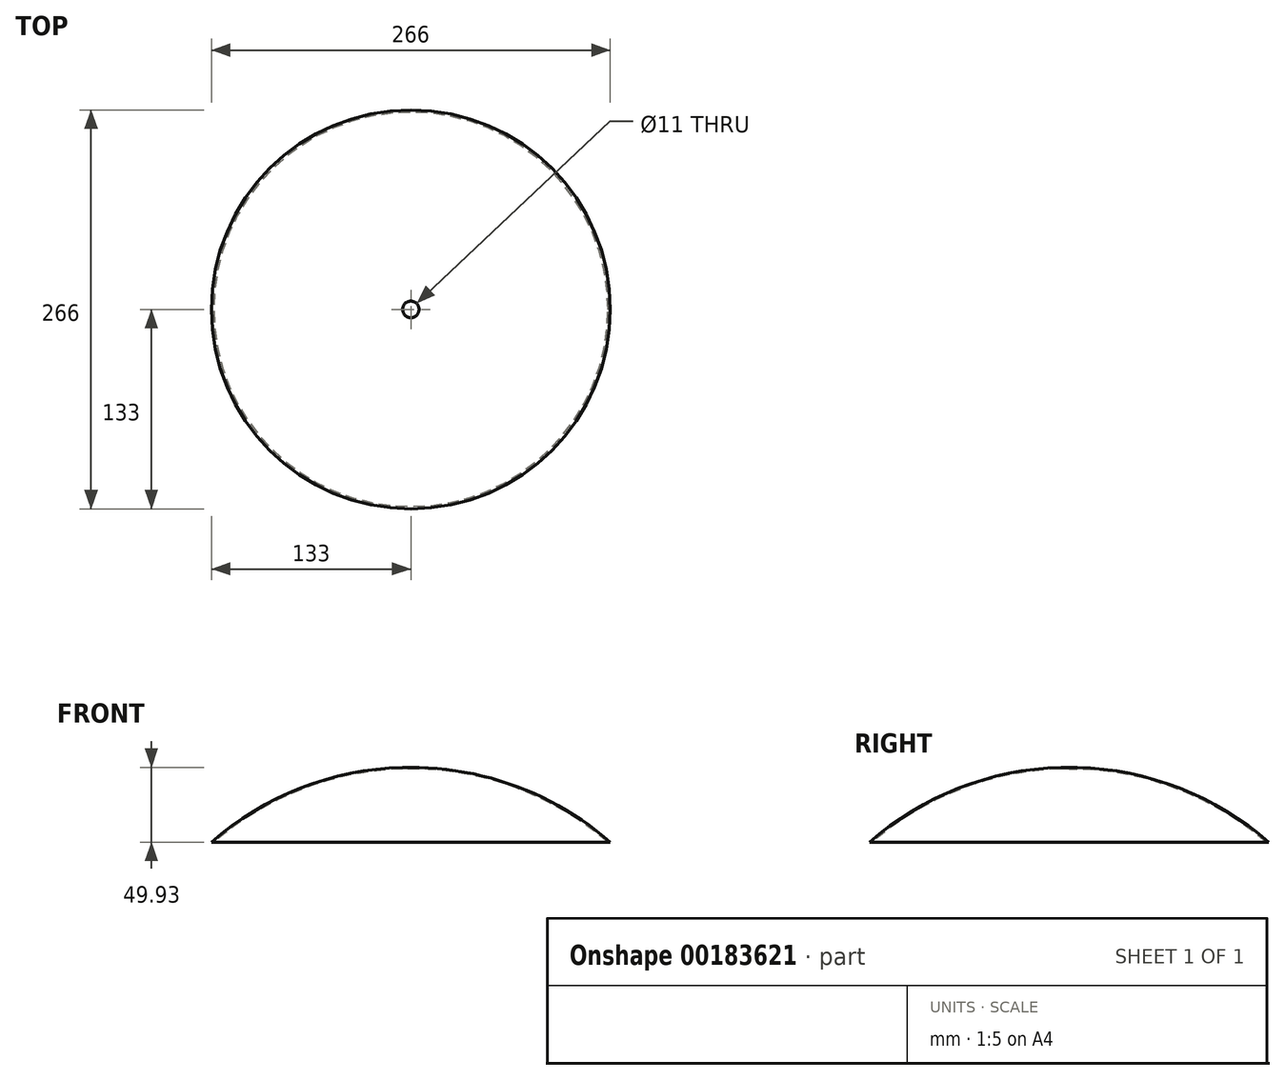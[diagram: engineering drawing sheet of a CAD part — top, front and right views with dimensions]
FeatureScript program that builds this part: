
annotation { "Feature Type Name" : "Feature", "Feature Type Description" : "" }
export const myFeature = defineFeature(function(context is Context, id is Id, definition is map)
    precondition{}
    {
        {
            var Q0;
            Q0=qCreatedBy(makeId("Front.planeOp"),FACE);
            var sketch = newSketch(context, id + "F0", { "sketchPlane" : qUnion([Q0])});
            skLineSegment(sketch, "E0.top", {"start": v(0, -25) * mm, "end": v(133, -25) * mm});
            skPoint(sketch, "E0.middle", {"position": v(0, 0) * mm});
            skArc(sketch, "E1", {"start": v(133, -25) * mm, "mid": v(71.04, 12.09) * mm, "end": v(0, 25) * mm});
            skPoint(sketch, "E1.second.point", {"position": v(0, 25) * mm});
            skLineSegment(sketch, "E2", {"start": v(0, 25) * mm, "end": v(0, -25) * mm});
            skSolve(sketch);
        }
        {
            var Q0;
            Q0 = qSketchRegion(id + "F0", true);
            var Q1;
            Q1=sQuery(id+"F0.wireOp",EDGE,"E2");
            revolve(context, id + "F1", {"entities" : qUnion([Q0]), "axis" : qUnion([Q1]), "revolveType" : RevolveType.FULL});
        }
        {
            var Q0;
            Q0=qCreatedBy(makeId("Top.planeOp"),FACE);
            var sketch = newSketch(context, id + "F2", { "sketchPlane" : qUnion([Q0])});
            skCircle(sketch, "E3", {"center": v(0, 0) * mm, "radius": 5.5 * mm});
            skSolve(sketch);
        }
        {
            var Q0;
            Q0=makeQuery(id+"F1.opRevolve","SWEPT_FACE",FACE,{"disambiguationData":[OSD([sQuery(id+"F0.wireOp",EDGE,"E0.top")])]});
            shell(context, id + "F3", {"entities" : qUnion([Q0]), "thickness" : 1 * mm});
        }
        {
            var Q0;
            Q0 = qSketchRegion(id + "F2", true);
            extrude(context, id + "F4", {"entities" : qUnion([Q0]), "operationType" : NewBodyOperationType.REMOVE, "endBound" : BoundingType.THROUGH_ALL, "depth" : 25 * mm});
        }
    });
